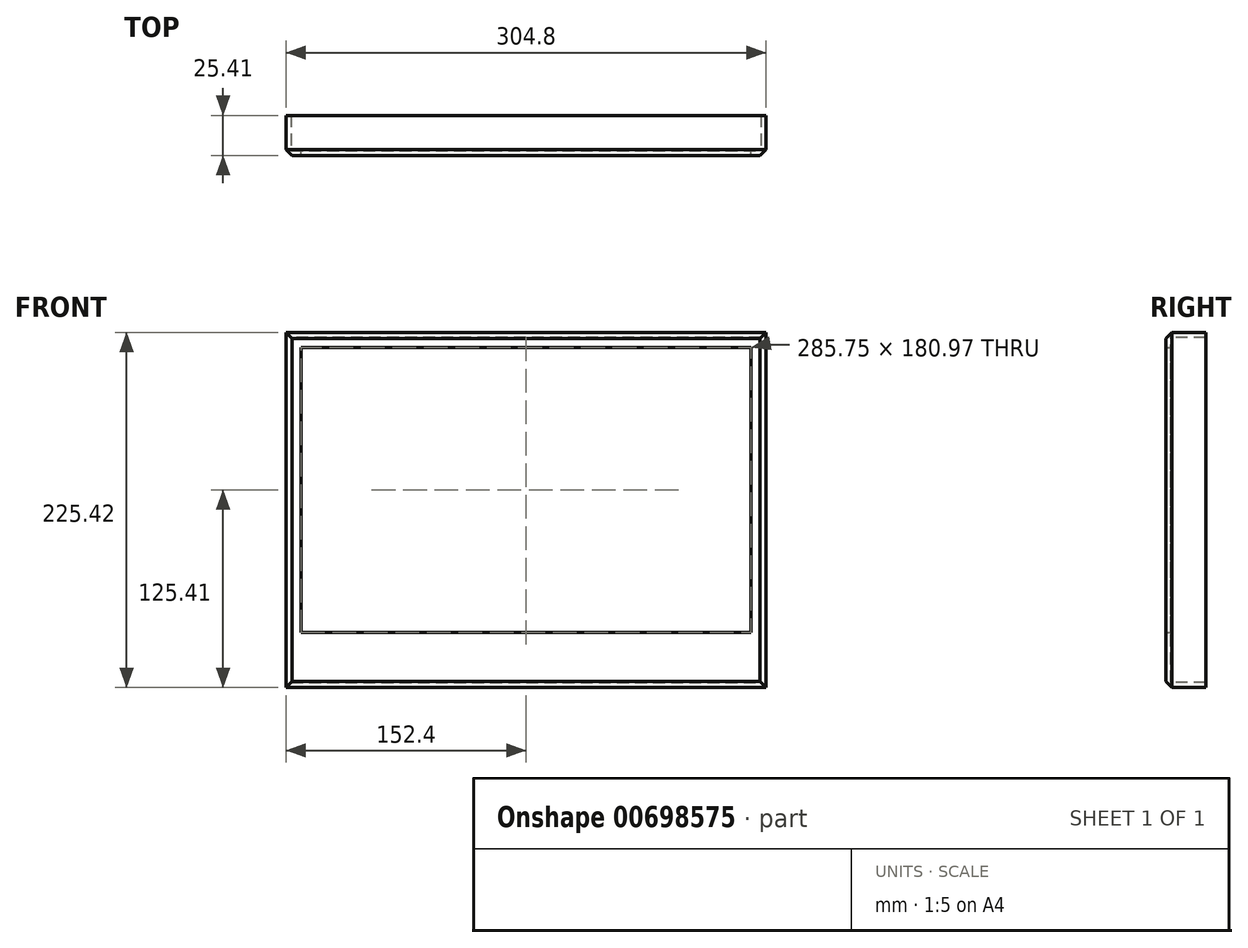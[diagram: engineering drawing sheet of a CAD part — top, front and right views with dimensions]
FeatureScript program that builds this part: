
annotation { "Feature Type Name" : "Feature", "Feature Type Description" : "" }
export const myFeature = defineFeature(function(context is Context, id is Id, definition is map)
    precondition{}
    {
        {
            var Q0;
            Q0=qCreatedBy(makeId("Front.planeOp"),FACE);
            var sketch = newSketch(context, id + "F0", { "sketchPlane" : qUnion([Q0])});
            skLineSegment(sketch, "E0.bottom", {"start": v(142.88, -90.49) * mm, "end": v(-142.88, -90.49) * mm});
            skLineSegment(sketch, "E0.top", {"start": v(142.88, 90.49) * mm, "end": v(-142.88, 90.49) * mm});
            skLineSegment(sketch, "E0.left", {"start": v(142.88, -90.49) * mm, "end": v(142.88, 90.49) * mm});
            skLineSegment(sketch, "E0.right", {"start": v(-142.88, -90.49) * mm, "end": v(-142.88, 90.49) * mm});
            skPoint(sketch, "E0.middle", {"position": v(0, 0) * mm});
            skLineSegment(sketch, "E1.bottom", {"start": v(149.23, -96.84) * mm, "end": v(-149.23, -96.84) * mm});
            skLineSegment(sketch, "E1.top", {"start": v(149.23, 96.84) * mm, "end": v(-149.23, 96.84) * mm});
            skLineSegment(sketch, "E1.left", {"start": v(149.23, -96.84) * mm, "end": v(149.23, 96.84) * mm});
            skLineSegment(sketch, "E1.right", {"start": v(-149.23, -96.84) * mm, "end": v(-149.23, 96.84) * mm});
            skLineSegment(sketch, "E2", {"start": v(-149.23, -96.84) * mm, "end": v(-149.23, -122.24) * mm});
            skLineSegment(sketch, "E3", {"start": v(-149.23, -122.24) * mm, "end": v(149.23, -122.24) * mm});
            skLineSegment(sketch, "E4", {"start": v(149.23, -122.24) * mm, "end": v(149.23, -96.84) * mm});
            skSolve(sketch);
        }
        {
            var Q0;
            Q0=makeQuery(id+"F0.imprint","IMPRINT",FACE,{"disambiguationData":[TD([[makeQuery(id+"F0.imprint","IMPRINT",EDGE,{"derivedFrom":sQuery(id+"F0.wireOp",EDGE,"E1.bottom")}),1.0]])]});
            var Q1;
            Q1=makeQuery(id+"F0.imprint","IMPRINT",FACE,{"disambiguationData":[TD([[makeQuery(id+"F0.imprint","IMPRINT",EDGE,{"derivedFrom":sQuery(id+"F0.wireOp",EDGE,"E0.bottom")}),1.0]])]});
            extrude(context, id + "F1", {"entities" : qUnion([Q0, Q1]), "depth" : 3.17 * mm, "offsetDistance" : 25.4 * mm});
        }
        {
            var Q0;
            Q0=makeQuery(id+"F1.opExtrude","CAP_FACE",FACE,{"disambiguationData":[OSD([sQuery(id+"F0.wireOp",EDGE,"E0.bottom"),sQuery(id+"F0.wireOp",EDGE,"E0.top"),sQuery(id+"F0.wireOp",EDGE,"E0.left"),sQuery(id+"F0.wireOp",EDGE,"E0.right"),sQuery(id+"F0.wireOp",EDGE,"E1.top"),sQuery(id+"F0.wireOp",EDGE,"E1.left"),sQuery(id+"F0.wireOp",EDGE,"E1.right"),sQuery(id+"F0.wireOp",EDGE,"E2"),sQuery(id+"F0.wireOp",EDGE,"E3"),sQuery(id+"F0.wireOp",EDGE,"E4")])],"isStart":false});
            var sketch = newSketch(context, id + "F2", { "sketchPlane" : qUnion([Q0])});
            skLineSegment(sketch, "E5.bottom", {"start": v(152.4, -125.41) * mm, "end": v(-152.4, -125.41) * mm});
            skLineSegment(sketch, "E5.top", {"start": v(152.4, 100.01) * mm, "end": v(-152.4, 100.01) * mm});
            skLineSegment(sketch, "E5.left", {"start": v(152.4, -125.41) * mm, "end": v(152.4, 100.01) * mm});
            skLineSegment(sketch, "E5.right", {"start": v(-152.4, -125.41) * mm, "end": v(-152.4, 100.01) * mm});
            skPoint(sketch, "E5.middle", {"position": v(0, -12.7) * mm});
            skLineSegment(sketch, "E6.bottom", {"start": v(-149.23, 96.84) * mm, "end": v(149.23, 96.84) * mm});
            skLineSegment(sketch, "E6.top", {"start": v(-149.23, -122.24) * mm, "end": v(149.23, -122.24) * mm});
            skLineSegment(sketch, "E6.left", {"start": v(-149.23, 96.84) * mm, "end": v(-149.23, -122.24) * mm});
            skLineSegment(sketch, "E6.right", {"start": v(149.23, 96.84) * mm, "end": v(149.23, -122.24) * mm});
            skSolve(sketch);
        }
        {
            var Q0;
            Q0=makeQuery(id+"F2.imprint","IMPRINT",FACE,{"disambiguationData":[TD([[makeQuery(id+"F2.imprint","IMPRINT",EDGE,{"derivedFrom":sQuery(id+"F2.wireOp",EDGE,"E5.bottom")}),-1.0]])]});
            extrude(context, id + "F3", {"entities" : qUnion([Q0]), "operationType" : NewBodyOperationType.ADD, "depth" : -25.4 * mm, "offsetDistance" : 25.4 * mm});
        }
        {
            var Q0;
            Q0=makeQuery(id+"F3.opExtrude","CAP_EDGE",EDGE,{"disambiguationData":[OSD([sQuery(id+"F2.wireOp",EDGE,"E5.right")])],"isStart":true});
            var Q1;
            Q1=makeQuery(id+"F3.opExtrude","CAP_EDGE",EDGE,{"disambiguationData":[OSD([sQuery(id+"F2.wireOp",EDGE,"E5.bottom")])],"isStart":true});
            var Q2;
            Q2=makeQuery(id+"F3.opExtrude","CAP_EDGE",EDGE,{"disambiguationData":[OSD([sQuery(id+"F2.wireOp",EDGE,"E5.left")])],"isStart":true});
            var Q3;
            Q3=makeQuery(id+"F3.opExtrude","CAP_EDGE",EDGE,{"disambiguationData":[OSD([sQuery(id+"F2.wireOp",EDGE,"E5.top")])],"isStart":true});
            chamfer(context, id + "F4", {"entities" : qUnion([Q0, Q1, Q2, Q3]), "width" : 3.8 * mm, "tangentPropagation" : true});
        }
    });
